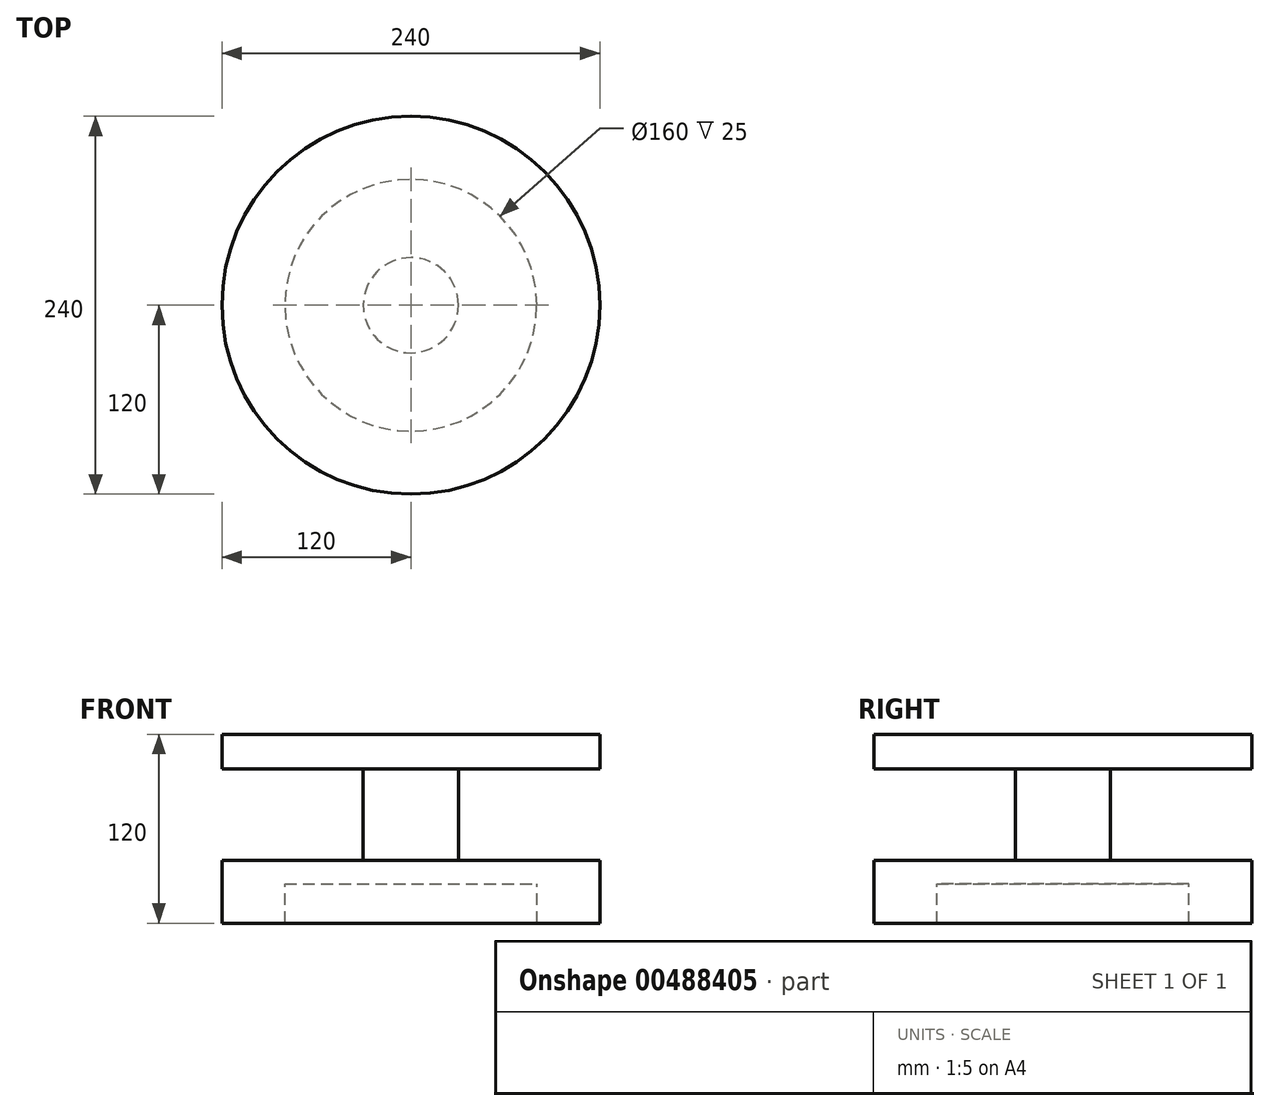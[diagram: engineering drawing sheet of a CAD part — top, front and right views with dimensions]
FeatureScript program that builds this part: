
annotation { "Feature Type Name" : "Feature", "Feature Type Description" : "" }
export const myFeature = defineFeature(function(context is Context, id is Id, definition is map)
    precondition{}
    {
        {
            var Q0;
            Q0=qCreatedBy(makeId("Top.planeOp"),FACE);
            var sketch = newSketch(context, id + "F0", { "sketchPlane" : qUnion([Q0])});
            skCircle(sketch, "E0", {"center": v(0, 0) * mm, "radius": 120 * mm});
            skCircle(sketch, "E1", {"center": v(0, 0) * mm, "radius": 100 * mm});
            skSolve(sketch);
        }
        {
            var Q0;
            Q0=makeQuery(id+"F0.imprint","IMPRINT",FACE,{"disambiguationData":[TD([[makeQuery(id+"F0.imprint","IMPRINT",EDGE,{"derivedFrom":sQuery(id+"F0.wireOp",EDGE,"E0")}),1.0]])]});
            var Q1;
            Q1=makeQuery(id+"F0.imprint","IMPRINT",FACE,{"disambiguationData":[TD([[makeQuery(id+"F0.imprint","IMPRINT",EDGE,{"derivedFrom":sQuery(id+"F0.wireOp",EDGE,"E1")}),1.0]])]});
            extrude(context, id + "F1", {"entities" : qUnion([Q0, Q1]), "oppositeDirection" : true, "depth" : 9 * mm});
        }
        {
            var Q0;
            Q0=makeQuery(id+"F0.imprint","IMPRINT",FACE,{"disambiguationData":[TD([[makeQuery(id+"F0.imprint","IMPRINT",EDGE,{"derivedFrom":sQuery(id+"F0.wireOp",EDGE,"E1")}),1.0]])]});
            extrude(context, id + "F2", {"entities" : qUnion([Q0]), "depth" : 4 * mm});
        }
        {
            var Q0;
            Q0=makeQuery(id+"F0.imprint","IMPRINT",FACE,{"disambiguationData":[TD([[makeQuery(id+"F0.imprint","IMPRINT",EDGE,{"derivedFrom":sQuery(id+"F0.wireOp",EDGE,"E0")}),1.0]])]});
            extrude(context, id + "F3", {"entities" : qUnion([Q0]), "operationType" : NewBodyOperationType.ADD, "depth" : 13 * mm});
        }
        {
            var Q0;
            Q0=makeQuery(id+"F2.opExtrude","CAP_FACE",FACE,{"disambiguationData":[OSD([sQuery(id+"F0.wireOp",EDGE,"E1")])],"isStart":false});
            extrude(context, id + "F4", {"entities" : qUnion([Q0]), "operationType" : NewBodyOperationType.ADD, "depth" : 9 * mm});
        }
        {
            var Q0;
            Q0=makeQuery(id+"F1.opExtrude","CAP_FACE",FACE,{"disambiguationData":[OSD([sQuery(id+"F0.wireOp",EDGE,"E0")])],"isStart":false});
            var sketch = newSketch(context, id + "F5", { "sketchPlane" : qUnion([Q0])});
            skCircle(sketch, "E2", {"center": v(0, 0) * mm, "radius": 30.25 * mm});
            skCircle(sketch, "E3", {"center": v(0, 0) * mm, "radius": 80 * mm});
            skSolve(sketch);
        }
        {
            var Q0;
            Q0=makeQuery(id+"F5.imprint","IMPRINT",FACE,{"disambiguationData":[TD([[makeQuery(id+"F5.imprint","IMPRINT",EDGE,{"derivedFrom":sQuery(id+"F5.wireOp",EDGE,"E2")}),1.0]])]});
            extrude(context, id + "F6", {"entities" : qUnion([Q0]), "operationType" : NewBodyOperationType.ADD, "depth" : 58 * mm});
        }
        {
            var Q0;
            {var subQ0=sQuery(id+"F0.wireOp",EDGE,"E1");Q0=makeQuery(id+"F4.boolean.opBoolean","MERGE",FACE,{"derivedFrom":[makeQuery(id+"F3.opExtrude","CAP_FACE",FACE,{"disambiguationData":[OSD([sQuery(id+"F0.wireOp",EDGE,"E0"),subQ0])],"isStart":false}),makeQuery(id+"F4.opExtrude","CAP_FACE",FACE,{"disambiguationData":[OSD([subQ0])],"isStart":false})]});}
            extrude(context, id + "F7", {"entities" : qUnion([Q0]), "operationType" : NewBodyOperationType.ADD, "oppositeDirection" : true, "depth" : 120 * mm, "hasSecondDirection" : true, "secondDirectionOppositeDirection" : true, "secondDirectionDepth" : 80 * mm});
        }
        {
            var Q0;
            Q0=makeQuery(id+"F5.imprint","IMPRINT",FACE,{"disambiguationData":[TD([[makeQuery(id+"F5.imprint","IMPRINT",EDGE,{"derivedFrom":sQuery(id+"F5.wireOp",EDGE,"E2")}),1.0]])]});
            var Q1;
            Q1=makeQuery(id+"F5.imprint","IMPRINT",FACE,{"disambiguationData":[TD([[makeQuery(id+"F5.imprint","IMPRINT",EDGE,{"derivedFrom":sQuery(id+"F5.wireOp",EDGE,"E2")}),-1.0]])]});
            extrude(context, id + "F8", {"entities" : qUnion([Q0, Q1]), "operationType" : NewBodyOperationType.REMOVE, "depth" : 98 * mm, "hasSecondDirection" : true, "secondDirectionOppositeDirection" : false, "secondDirectionDepth" : 73 * mm});
        }
    });
